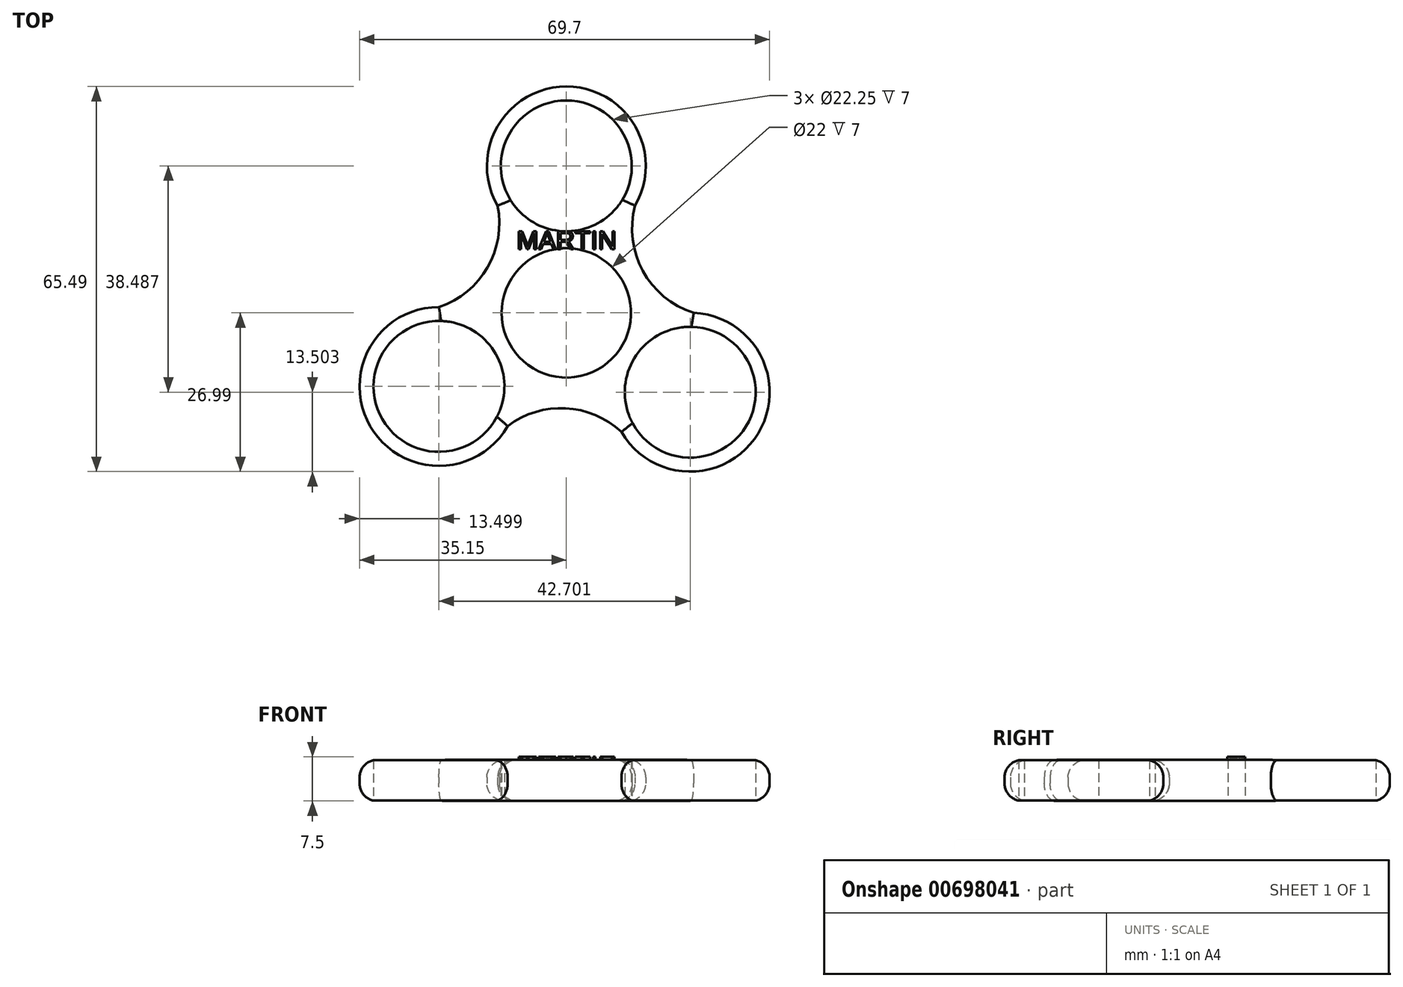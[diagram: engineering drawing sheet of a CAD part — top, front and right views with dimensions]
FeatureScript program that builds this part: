
annotation { "Feature Type Name" : "Feature", "Feature Type Description" : "" }
export const myFeature = defineFeature(function(context is Context, id is Id, definition is map)
    precondition{}
    {
        {
            var Q0;
            Q0=qCreatedBy(makeId("Top.planeOp"),FACE);
            var sketch = newSketch(context, id + "F0", { "sketchPlane" : qUnion([Q0]), "disableImprinting" : false});
            skCircle(sketch, "E0", {"center": v(0, 0) * mm, "radius": 11 * mm});
            skCircle(sketch, "E1", {"center": v(0, 25) * mm, "radius": 11.12 * mm});
            skCircle(sketch, "E2", {"center": v(21.05, -13.49) * mm, "radius": 11.12 * mm});
            skCircle(sketch, "E3", {"center": v(-21.65, -12.5) * mm, "radius": 11.12 * mm});
            skArc(sketch, "E4", {"start": v(-21.65, 1) * mm, "mid": v(-33.34, -19.25) * mm, "end": v(-9.96, -19.25) * mm});
            skArc(sketch, "E5", {"start": v(9.36, -20.24) * mm, "mid": v(32.59, -20.5) * mm, "end": v(21.65, 0) * mm});
            skArc(sketch, "E6", {"start": v(11.7, 18.25) * mm, "mid": v(0, 38.5) * mm, "end": v(-11.7, 18.25) * mm});
            skArc(sketch, "E7", {"start": v(-21.65, 1) * mm, "mid": v(-13.4, 7.73) * mm, "end": v(-11.7, 18.25) * mm});
            skArc(sketch, "E8", {"start": v(11.7, 18.25) * mm, "mid": v(13, 7.12) * mm, "end": v(21.65, 0) * mm});
            skArc(sketch, "E9", {"start": v(9.36, -20.24) * mm, "mid": v(-0.12, -16.21) * mm, "end": v(-9.96, -19.25) * mm});
            skSolve(sketch);
        }
        {
            var Q0;
            Q0=makeQuery(id+"F0.imprint","IMPRINT",FACE,{"disambiguationData":[TD([[makeQuery(id+"F0.imprint","IMPRINT",EDGE,{"derivedFrom":sQuery(id+"F0.wireOp",EDGE,"E0")}),-1.0]])]});
            extrude(context, id + "F1", {"entities" : qUnion([Q0]), "depth" : 7 * mm, "offsetDistance" : 25 * mm});
        }
        {
            var Q0;
            Q0=makeQuery(id+"F1.opExtrude","CAP_EDGE",EDGE,{"disambiguationData":[OSD([sQuery(id+"F0.wireOp",EDGE,"E4")])],"isStart":false});
            var Q1;
            Q1=makeQuery(id+"F1.opExtrude","CAP_EDGE",EDGE,{"disambiguationData":[OSD([sQuery(id+"F0.wireOp",EDGE,"E9")])],"isStart":false});
            var Q2;
            Q2=makeQuery(id+"F1.opExtrude","CAP_EDGE",EDGE,{"disambiguationData":[OSD([sQuery(id+"F0.wireOp",EDGE,"E5")])],"isStart":false});
            var Q3;
            Q3=makeQuery(id+"F1.opExtrude","CAP_EDGE",EDGE,{"disambiguationData":[OSD([sQuery(id+"F0.wireOp",EDGE,"E8")])],"isStart":false});
            var Q4;
            Q4=makeQuery(id+"F1.opExtrude","CAP_EDGE",EDGE,{"disambiguationData":[OSD([sQuery(id+"F0.wireOp",EDGE,"E6")])],"isStart":false});
            var Q5;
            Q5=makeQuery(id+"F1.opExtrude","CAP_EDGE",EDGE,{"disambiguationData":[OSD([sQuery(id+"F0.wireOp",EDGE,"E7")])],"isStart":false});
            var Q6;
            Q6=makeQuery(id+"F1.opExtrude","CAP_EDGE",EDGE,{"disambiguationData":[OSD([sQuery(id+"F0.wireOp",EDGE,"E6")])],"isStart":true});
            var Q7;
            Q7=makeQuery(id+"F1.opExtrude","CAP_EDGE",EDGE,{"disambiguationData":[OSD([sQuery(id+"F0.wireOp",EDGE,"E8")])],"isStart":true});
            var Q8;
            Q8=makeQuery(id+"F1.opExtrude","CAP_EDGE",EDGE,{"disambiguationData":[OSD([sQuery(id+"F0.wireOp",EDGE,"E5")])],"isStart":true});
            var Q9;
            Q9=makeQuery(id+"F1.opExtrude","CAP_EDGE",EDGE,{"disambiguationData":[OSD([sQuery(id+"F0.wireOp",EDGE,"E9")])],"isStart":true});
            var Q10;
            Q10=makeQuery(id+"F1.opExtrude","CAP_EDGE",EDGE,{"disambiguationData":[OSD([sQuery(id+"F0.wireOp",EDGE,"E4")])],"isStart":true});
            var Q11;
            Q11=makeQuery(id+"F1.opExtrude","CAP_EDGE",EDGE,{"disambiguationData":[OSD([sQuery(id+"F0.wireOp",EDGE,"E7")])],"isStart":true});
            fillet(context, id + "F2", {"entities" : qUnion([Q0, Q1, Q2, Q3, Q4, Q5, Q6, Q7, Q8, Q9, Q10, Q11]), "radius" : 3 * mm, "tangentPropagation" : true, "allowEdgeOverflow" : false});
        }
        {
            var Q0;
            Q0=makeQuery(id+"F1.opExtrude","CAP_FACE",FACE,{"disambiguationData":[OSD([sQuery(id+"F0.wireOp",EDGE,"E0"),sQuery(id+"F0.wireOp",EDGE,"E1"),sQuery(id+"F0.wireOp",EDGE,"E2"),sQuery(id+"F0.wireOp",EDGE,"E3"),sQuery(id+"F0.wireOp",EDGE,"E4"),sQuery(id+"F0.wireOp",EDGE,"E5"),sQuery(id+"F0.wireOp",EDGE,"E6"),sQuery(id+"F0.wireOp",EDGE,"E7"),sQuery(id+"F0.wireOp",EDGE,"E8"),sQuery(id+"F0.wireOp",EDGE,"E9")])],"isStart":false});
            var sketch = newSketch(context, id + "F3", { "sketchPlane" : qUnion([Q0])});
            skText(sketch, "E10", { "text": "MARTIN", "fontName": "Arimo-Regular.ttf"});
            skPoint(sketch, "E11", {"position": v(-0.05, 14) * mm});
            const initialGuessF3  = {"E10": [-0.00842, 0.01085, 1, 0, 0.00319]};
            skSetInitialGuess(sketch, initialGuessF3);
            skSolve(sketch);
        }
        {
            var Q0;
            Q0 = qSketchRegion(id + "F3", true);
            extrude(context, id + "F4", {"entities" : qUnion([Q0]), "operationType" : NewBodyOperationType.ADD, "depth" : .5 * mm, "offsetDistance" : 25 * mm});
        }
    });
